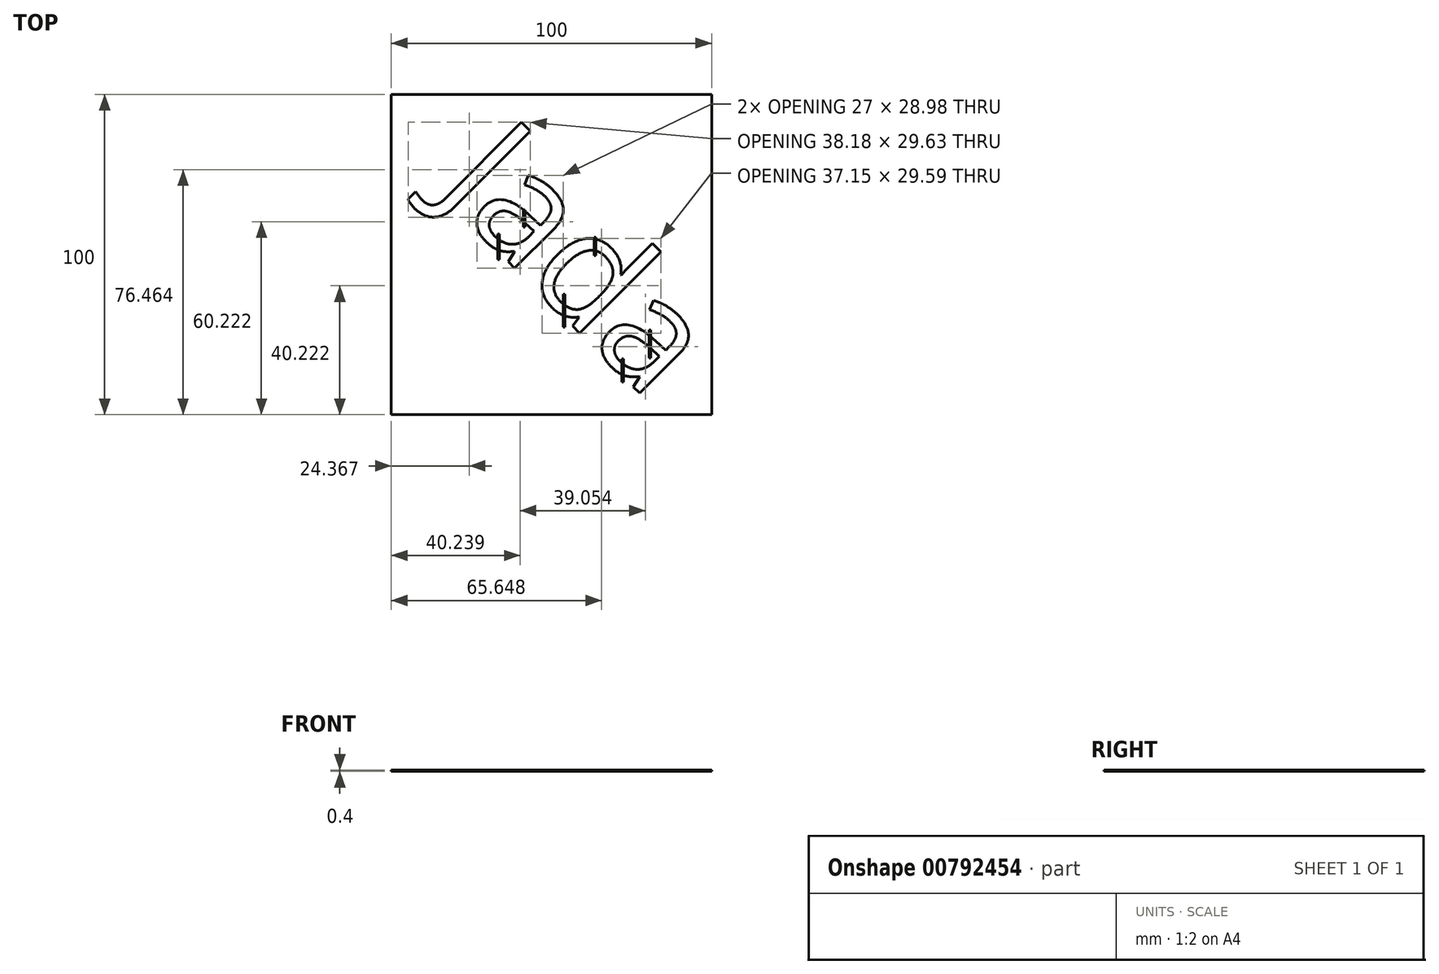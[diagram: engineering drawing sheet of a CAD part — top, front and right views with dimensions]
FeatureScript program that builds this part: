
annotation { "Feature Type Name" : "Feature", "Feature Type Description" : "" }
export const myFeature = defineFeature(function(context is Context, id is Id, definition is map)
    precondition{}
    {
        {
            var Q0;
            Q0=qCreatedBy(makeId("Top.planeOp"),FACE);
            var sketch = newSketch(context, id + "F0", { "sketchPlane" : qUnion([Q0])});
            skLineSegment(sketch, "E0.bottom", {"start": v(50, 50) * mm, "end": v(-50, 50) * mm});
            skLineSegment(sketch, "E0.top", {"start": v(50, -50) * mm, "end": v(-50, -50) * mm});
            skLineSegment(sketch, "E0.left", {"start": v(50, 50) * mm, "end": v(50, -50) * mm});
            skLineSegment(sketch, "E0.right", {"start": v(-50, 50) * mm, "end": v(-50, -50) * mm});
            skPoint(sketch, "E0.middle", {"position": v(0, 0) * mm});
            skSolve(sketch);
        }
        {
            var Q0;
            Q0=makeQuery(id+"F0.imprint","IMPRINT",FACE,{"disambiguationData":[TD([[makeQuery(id+"F0.imprint","IMPRINT",EDGE,{"derivedFrom":sQuery(id+"F0.wireOp",EDGE,"E0.bottom")}),1.0]])]});
            extrude(context, id + "F1", {"entities" : qUnion([Q0]), "depth" : .4 * mm, "offsetDistance" : 25 * mm});
        }
        {
            var Q0;
            Q0=makeQuery(id+"F1.opExtrude","CAP_FACE",FACE,{"disambiguationData":[OSD([sQuery(id+"F0.wireOp",EDGE,"E0.bottom"),sQuery(id+"F0.wireOp",EDGE,"E0.top"),sQuery(id+"F0.wireOp",EDGE,"E0.left"),sQuery(id+"F0.wireOp",EDGE,"E0.right")])],"isStart":false});
            var sketch = newSketch(context, id + "F2", { "sketchPlane" : qUnion([Q0])});
            skText(sketch, "E1", { "text": "Jada", "fontName": "OpenSans-Regular.ttf"});
            const initialGuessF2  = {"E1": [-0.03627, 0.02053, 0.7071, -0.7071, 0.03402]};
            skSetInitialGuess(sketch, initialGuessF2);
            skSolve(sketch);
        }
        {
            var Q0;
            Q0 = qSketchRegion(id + "F2", true);
            extrude(context, id + "F3", {"entities" : qUnion([Q0]), "operationType" : NewBodyOperationType.REMOVE, "oppositeDirection" : true, "depth" : 25 * mm, "offsetDistance" : 25 * mm});
        }
        {
            var Q0;
            Q0=qCreatedBy(makeId("Top.planeOp"),FACE);
            var sketch = newSketch(context, id + "F4", { "sketchPlane" : qUnion([Q0])});
            skPoint(sketch, "E2.oppositeSnap0", {"position": v(-6.8, 8.54) * mm});
            skLineSegment(sketch, "E2.bottom", {"start": v(-8.7, 13.92) * mm, "end": v(-8.2, 13.92) * mm});
            skLineSegment(sketch, "E2.top", {"start": v(-8.7, 8.54) * mm, "end": v(-8.2, 8.54) * mm});
            skLineSegment(sketch, "E2.left", {"start": v(-8.7, 13.92) * mm, "end": v(-8.7, 8.54) * mm});
            skLineSegment(sketch, "E2.right", {"start": v(-8.2, 13.92) * mm, "end": v(-8.2, 8.54) * mm});
            skLineSegment(sketch, "E3.bottom", {"start": v(13.4, 5.43) * mm, "end": v(13.9, 5.43) * mm});
            skLineSegment(sketch, "E3.top", {"start": v(13.4, -0.34) * mm, "end": v(13.9, -0.34) * mm});
            skLineSegment(sketch, "E3.left", {"start": v(13.4, 5.43) * mm, "end": v(13.4, -0.34) * mm});
            skLineSegment(sketch, "E3.right", {"start": v(13.9, 5.43) * mm, "end": v(13.9, -0.34) * mm});
            skLineSegment(sketch, "E4.bottom", {"start": v(30.47, -23.61) * mm, "end": v(30.97, -23.61) * mm});
            skLineSegment(sketch, "E4.top", {"start": v(30.47, -32.38) * mm, "end": v(30.97, -32.38) * mm});
            skLineSegment(sketch, "E4.left", {"start": v(30.47, -23.61) * mm, "end": v(30.47, -32.38) * mm});
            skLineSegment(sketch, "E4.right", {"start": v(30.97, -23.61) * mm, "end": v(30.97, -32.38) * mm});
            skLineSegment(sketch, "E5.bottom", {"start": v(-16.73, 6.34) * mm, "end": v(-16.23, 6.34) * mm});
            skLineSegment(sketch, "E5.top", {"start": v(-16.73, -1.62) * mm, "end": v(-16.23, -1.62) * mm});
            skLineSegment(sketch, "E5.left", {"start": v(-16.73, 6.34) * mm, "end": v(-16.73, -1.62) * mm});
            skLineSegment(sketch, "E5.right", {"start": v(-16.23, 6.34) * mm, "end": v(-16.23, -1.62) * mm});
            skLineSegment(sketch, "E6.bottom", {"start": v(3.72, -12.44) * mm, "end": v(4.22, -12.44) * mm});
            skLineSegment(sketch, "E6.top", {"start": v(3.72, -22.7) * mm, "end": v(4.22, -22.7) * mm});
            skLineSegment(sketch, "E6.left", {"start": v(3.72, -12.44) * mm, "end": v(3.72, -22.7) * mm});
            skLineSegment(sketch, "E6.right", {"start": v(4.22, -12.44) * mm, "end": v(4.22, -22.7) * mm});
            skLineSegment(sketch, "E7.bottom", {"start": v(21.94, -32.65) * mm, "end": v(22.44, -32.65) * mm});
            skLineSegment(sketch, "E7.top", {"start": v(21.94, -39.9) * mm, "end": v(22.44, -39.9) * mm});
            skLineSegment(sketch, "E7.left", {"start": v(21.94, -32.65) * mm, "end": v(21.94, -39.9) * mm});
            skLineSegment(sketch, "E7.right", {"start": v(22.44, -32.65) * mm, "end": v(22.44, -39.9) * mm});
            skSolve(sketch);
        }
        {
            var Q0;
            Q0 = qSketchRegion(id + "F4", true);
            extrude(context, id + "F5", {"entities" : qUnion([Q0]), "depth" : .4 * mm, "offsetDistance" : 25 * mm});
        }
    });
